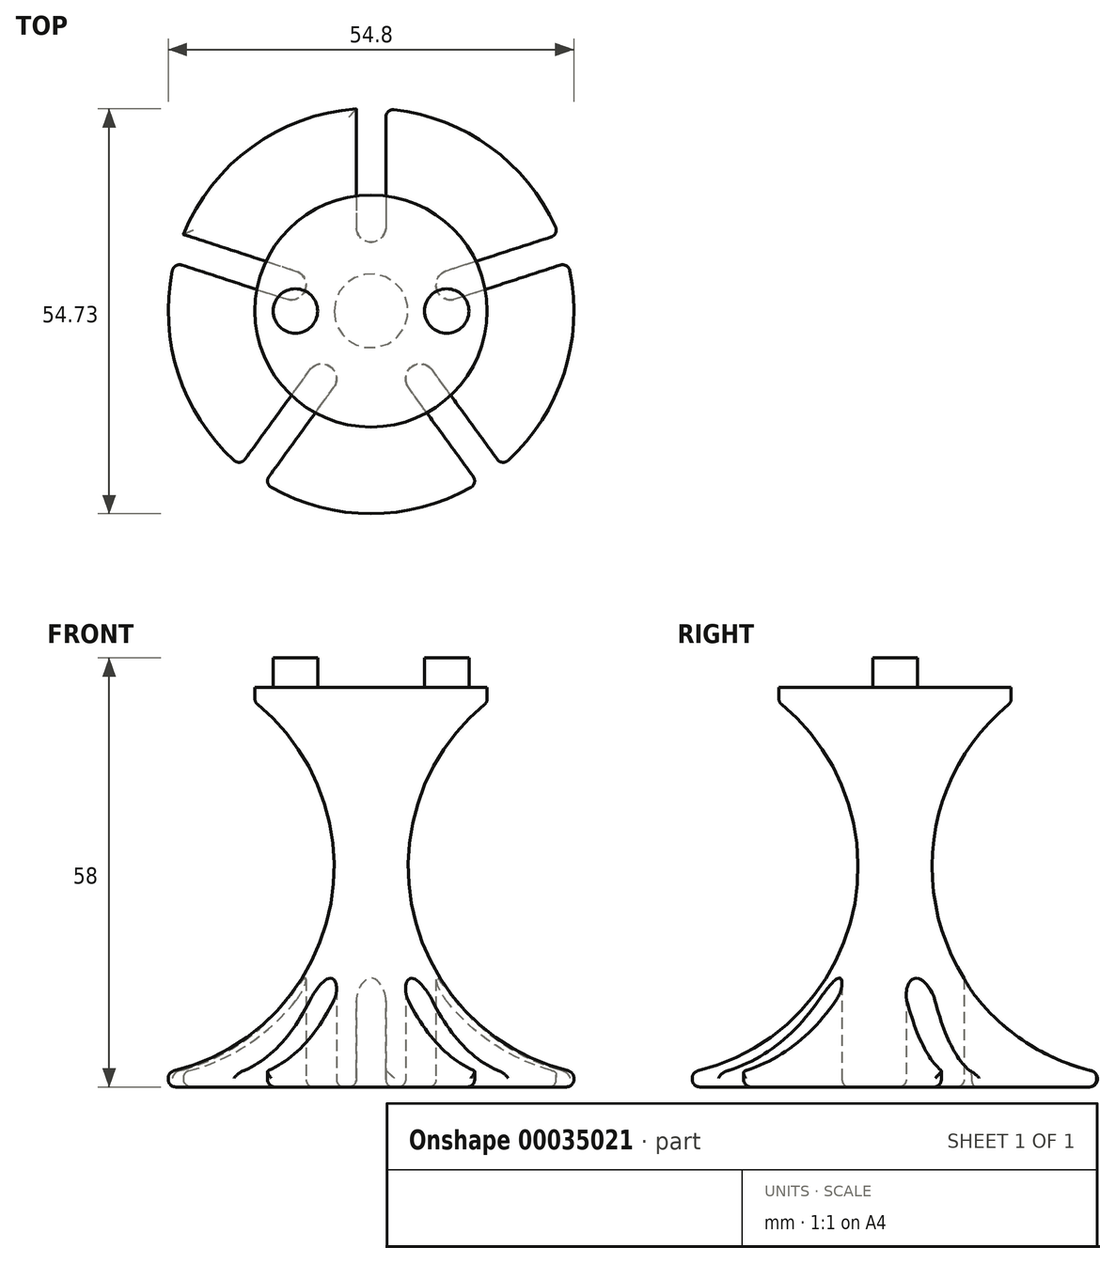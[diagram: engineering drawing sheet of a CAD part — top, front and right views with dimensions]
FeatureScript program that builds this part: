
annotation { "Feature Type Name" : "Feature", "Feature Type Description" : "" }
export const myFeature = defineFeature(function(context is Context, id is Id, definition is map)
    precondition{}
    {
        {
            var Q0;
            Q0=qCreatedBy(makeId("Front.planeOp"),FACE);
            var sketch = newSketch(context, id + "F0", { "sketchPlane" : qUnion([Q0])});
            skArc(sketch, "E0", {"start": v(-27.4, 0) * mm, "mid": v(-5.75, 21.3) * mm, "end": v(-15.7, 50) * mm});
            skLineSegment(sketch, "E1", {"start": v(-27.4, 0) * mm, "end": v(27.4, 0) * mm});
            skLineSegment(sketch, "E2", {"start": v(0, 0) * mm, "end": v(0, 50) * mm});
            skArc(sketch, "E3.MirrorCS", {"start": v(27.4, 0) * mm, "mid": v(5.75, 21.3) * mm, "end": v(15.7, 50) * mm});
            skLineSegment(sketch, "E4", {"start": v(15.7, 50) * mm, "end": v(-15.7, 50) * mm});
            skLineSegment(sketch, "E5", {"start": v(5.75, 21.3) * mm, "end": v(-5.75, 21.3) * mm, "construction": true});
            skLineSegment(sketch, "E6", {"start": v(-33.43, 27.78) * mm, "end": v(-33.43, 38) * mm, "construction": true});
            skSolve(sketch);
        }
        {
            var Q0;
            {var subQ1=sQuery(id+"F0.wireOp",EDGE,"E2");Q0=makeQuery(id+"F0.imprint","IMPRINT",FACE,{"disambiguationData":[TD([[makeQuery(id+"F0.imprint","IMPRINT",EDGE,{"derivedFrom":subQ1}),1.0]])]});}
            var Q1;
            Q1=sQuery(id+"F0.wireOp",EDGE,"E2");
            revolve(context, id + "F1", {"entities" : qUnion([Q0]), "axis" : qUnion([Q1]), "revolveType" : RevolveType.FULL});
        }
        {
            var Q0;
            Q0=makeQuery(id+"F1.opRevolve","SWEPT_FACE",FACE,{"disambiguationData":[OSD([sQuery(id+"F0.wireOp",EDGE,"E4")])]});
            var sketch = newSketch(context, id + "F2", { "sketchPlane" : qUnion([Q0])});
            skCircle(sketch, "E7", {"center": v(-10.22, 0) * mm, "radius": 3 * mm});
            skLineSegment(sketch, "E8", {"start": v(-7.22, 0) * mm, "end": v(0, 0) * mm, "construction": true});
            skCircle(sketch, "E9", {"center": v(10.22, 0) * mm, "radius": 3 * mm});
            skLineSegment(sketch, "E10", {"start": v(0, 0) * mm, "end": v(7.22, 0) * mm, "construction": true});
            skLineSegment(sketch, "E11", {"start": v(-8.9, 0) * mm, "end": v(-5.9, 0) * mm, "construction": true});
            skSolve(sketch);
        }
        {
            var Q0;
            Q0=makeQuery(id+"F2.imprint","IMPRINT",FACE,{"disambiguationData":[TD([[makeQuery(id+"F2.imprint","IMPRINT",EDGE,{"derivedFrom":sQuery(id+"F2.wireOp",EDGE,"E9")}),1.0]])]});
            var Q1;
            Q1=makeQuery(id+"F2.imprint","IMPRINT",FACE,{"disambiguationData":[TD([[makeQuery(id+"F2.imprint","IMPRINT",EDGE,{"derivedFrom":sQuery(id+"F2.wireOp",EDGE,"E7")}),1.0]])]});
            extrude(context, id + "F3", {"entities" : qUnion([Q0, Q1]), "operationType" : NewBodyOperationType.ADD, "depth" : 6 * mm});
        }
        {
            var Q0;
            Q0=makeQuery(id+"F1.opRevolve","SWEPT_FACE",FACE,{"disambiguationData":[OSD([sQuery(id+"F0.wireOp",EDGE,"E4")])]});
            extrude(context, id + "F4", {"entities" : qUnion([Q0]), "operationType" : NewBodyOperationType.ADD, "depth" : 2 * mm});
        }
        {
            var Q0;
            Q0=makeQuery(id+"F1.opRevolve","SWEPT_FACE",FACE,{"disambiguationData":[OSD([sQuery(id+"F0.wireOp",EDGE,"E1")])]});
            extrude(context, id + "F5", {"entities" : qUnion([Q0]), "operationType" : NewBodyOperationType.ADD, "depth" : 2 * mm});
        }
        {
            var Q0;
            Q0=makeQuery(id+"F5.opExtrude","CAP_FACE",FACE,{"disambiguationData":[OSD([sQuery(id+"F0.wireOp",EDGE,"E1")])],"isStart":false});
            var sketch = newSketch(context, id + "F6", { "sketchPlane" : qUnion([Q0])});
            skLineSegment(sketch, "E12", {"start": v(0, 0) * mm, "end": v(0, -27.4) * mm, "construction": true});
            skLineSegment(sketch, "E13", {"start": v(-2, -27.33) * mm, "end": v(-2, -11.33) * mm});
            skLineSegment(sketch, "E14", {"start": v(2, -27.33) * mm, "end": v(2, -11.33) * mm});
            skArc(sketch, "E15", {"start": v(2, -11.33) * mm, "mid": v(0, -9.33) * mm, "end": v(-2, -11.33) * mm});
            skLineSegment(sketch, "E16.1.0", {"start": v(25.37, -10.35) * mm, "end": v(10.15, -5.4) * mm});
            skArc(sketch, "E16.1.1", {"start": v(11.4, -1.6) * mm, "mid": v(8.87, -2.88) * mm, "end": v(10.15, -5.4) * mm});
            skLineSegment(sketch, "E16.1.2", {"start": v(26.6, -6.54) * mm, "end": v(11.4, -1.6) * mm});
            skLineSegment(sketch, "E16.2.0", {"start": v(17.68, 20.93) * mm, "end": v(8.28, 7.99) * mm});
            skArc(sketch, "E16.2.1", {"start": v(5.04, 10.34) * mm, "mid": v(5.48, 7.55) * mm, "end": v(8.28, 7.99) * mm});
            skLineSegment(sketch, "E16.2.2", {"start": v(14.44, 23.28) * mm, "end": v(5.04, 10.34) * mm});
            skLineSegment(sketch, "E16.3.0", {"start": v(-14.44, 23.28) * mm, "end": v(-5.04, 10.34) * mm});
            skArc(sketch, "E16.3.1", {"start": v(-8.28, 7.99) * mm, "mid": v(-5.48, 7.55) * mm, "end": v(-5.04, 10.34) * mm});
            skLineSegment(sketch, "E16.3.2", {"start": v(-17.68, 20.93) * mm, "end": v(-8.28, 7.99) * mm});
            skLineSegment(sketch, "E16.4.0", {"start": v(-26.6, -6.54) * mm, "end": v(-11.4, -1.6) * mm});
            skArc(sketch, "E16.4.1", {"start": v(-10.15, -5.4) * mm, "mid": v(-8.87, -2.88) * mm, "end": v(-11.4, -1.6) * mm});
            skLineSegment(sketch, "E16.4.2", {"start": v(-25.37, -10.35) * mm, "end": v(-10.15, -5.4) * mm});
            skPoint(sketch, "E16.center", {"position": v(0, 0) * mm});
            skSolve(sketch);
        }
        {
            var Q0;
            Q0 = qSketchRegion(id + "F6", true);
            var Q1;
            {var subQ2=sQuery(id+"F6.wireOp",EDGE,"E16.4.0");Q1=makeQuery(id+"F6.imprint","IMPRINT",FACE,{"disambiguationData":[TD([[makeQuery(id+"F6.imprint","IMPRINT",EDGE,{"derivedFrom":subQ2}),-1.0]])]});}
            var Q2;
            {var subQ2=sQuery(id+"F6.wireOp",EDGE,"E16.3.0");Q2=makeQuery(id+"F6.imprint","IMPRINT",FACE,{"disambiguationData":[TD([[makeQuery(id+"F6.imprint","IMPRINT",EDGE,{"derivedFrom":subQ2}),-1.0]])]});}
            var Q3;
            {var subQ2=sQuery(id+"F6.wireOp",EDGE,"E16.2.0");Q3=makeQuery(id+"F6.imprint","IMPRINT",FACE,{"disambiguationData":[TD([[makeQuery(id+"F6.imprint","IMPRINT",EDGE,{"derivedFrom":subQ2}),-1.0]])]});}
            var Q4;
            {var subQ2=sQuery(id+"F6.wireOp",EDGE,"E16.1.0");Q4=makeQuery(id+"F6.imprint","IMPRINT",FACE,{"disambiguationData":[TD([[makeQuery(id+"F6.imprint","IMPRINT",EDGE,{"derivedFrom":subQ2}),-1.0]])]});}
            var Q5;
            {var subQ2=sQuery(id+"F6.wireOp",EDGE,"E13");Q5=makeQuery(id+"F6.imprint","IMPRINT",FACE,{"disambiguationData":[TD([[makeQuery(id+"F6.imprint","IMPRINT",EDGE,{"derivedFrom":subQ2}),-1.0]])]});}
            extrude(context, id + "F7", {"entities" : qUnion([Q0, Q1, Q2, Q3, Q4, Q5]), "operationType" : NewBodyOperationType.REMOVE, "endBound" : BoundingType.UP_TO_NEXT, "oppositeDirection" : true, "depth" : 25 * mm});
        }
        {
            var Q0;
            {var subQ0=sQuery(id+"F0.wireOp",EDGE,"E0");var subQ1=sQuery(id+"F0.wireOp",EDGE,"E4");Q0=makeQuery(id+"F4.boolean.opBoolean","MERGE",EDGE,{"derivedFrom":[makeQuery(id+"F1.opRevolve","SWEPT_EDGE",EDGE,{"disambiguationData":[OSD([subQ0,subQ1])]}),makeQuery(id+"F4.opExtrude","CAP_EDGE",EDGE,{"disambiguationData":[OSD([subQ0,subQ1])],"isStart":true})]});}
            var Q1;
            Q1=makeQuery(id+"F5.opExtrude","CAP_FACE",FACE,{"disambiguationData":[OSD([sQuery(id+"F0.wireOp",EDGE,"E1")])],"isStart":false});
            var Q2;
            {var subQ0=sQuery(id+"F0.wireOp",EDGE,"E0");var subQ1=sQuery(id+"F0.wireOp",EDGE,"E1");Q2=makeQuery(id+"F7.boolean.opBoolean","SPLIT",EDGE,{"disambiguationData":[TD([makeQuery(id+"F7.opExtrude","SWEPT_FACE",FACE,{"disambiguationData":[OSD([sQuery(id+"F6.wireOp",EDGE,"E16.3.2")])]})])],"derivedFrom":makeQuery(id+"F5.boolean.opBoolean","MERGE",EDGE,{"derivedFrom":[makeQuery(id+"F1.opRevolve","SWEPT_EDGE",EDGE,{"disambiguationData":[OSD([subQ0,subQ1])]}),makeQuery(id+"F5.opExtrude","CAP_EDGE",EDGE,{"disambiguationData":[OSD([subQ0,subQ1])],"isStart":true})]})});}
            var Q3;
            {var subQ0=sQuery(id+"F0.wireOp",EDGE,"E0");var subQ1=sQuery(id+"F0.wireOp",EDGE,"E1");Q3=makeQuery(id+"F7.boolean.opBoolean","SPLIT",EDGE,{"disambiguationData":[TD([makeQuery(id+"F7.opExtrude","SWEPT_FACE",FACE,{"disambiguationData":[OSD([sQuery(id+"F6.wireOp",EDGE,"E16.2.2")])]})])],"derivedFrom":makeQuery(id+"F5.boolean.opBoolean","MERGE",EDGE,{"derivedFrom":[makeQuery(id+"F1.opRevolve","SWEPT_EDGE",EDGE,{"disambiguationData":[OSD([subQ0,subQ1])]}),makeQuery(id+"F5.opExtrude","CAP_EDGE",EDGE,{"disambiguationData":[OSD([subQ0,subQ1])],"isStart":true})]})});}
            var Q4;
            {var subQ0=sQuery(id+"F0.wireOp",EDGE,"E0");var subQ1=sQuery(id+"F0.wireOp",EDGE,"E1");Q4=makeQuery(id+"F7.boolean.opBoolean","SPLIT",EDGE,{"disambiguationData":[TD([makeQuery(id+"F7.opExtrude","SWEPT_FACE",FACE,{"disambiguationData":[OSD([sQuery(id+"F6.wireOp",EDGE,"E16.1.2")])]})])],"derivedFrom":makeQuery(id+"F5.boolean.opBoolean","MERGE",EDGE,{"derivedFrom":[makeQuery(id+"F1.opRevolve","SWEPT_EDGE",EDGE,{"disambiguationData":[OSD([subQ0,subQ1])]}),makeQuery(id+"F5.opExtrude","CAP_EDGE",EDGE,{"disambiguationData":[OSD([subQ0,subQ1])],"isStart":true})]})});}
            var Q5;
            {var subQ0=sQuery(id+"F0.wireOp",EDGE,"E0");var subQ1=sQuery(id+"F0.wireOp",EDGE,"E1");Q5=makeQuery(id+"F7.boolean.opBoolean","SPLIT",EDGE,{"disambiguationData":[TD([makeQuery(id+"F7.opExtrude","SWEPT_FACE",FACE,{"disambiguationData":[OSD([sQuery(id+"F6.wireOp",EDGE,"E14")])]})])],"derivedFrom":makeQuery(id+"F5.boolean.opBoolean","MERGE",EDGE,{"derivedFrom":[makeQuery(id+"F1.opRevolve","SWEPT_EDGE",EDGE,{"disambiguationData":[OSD([subQ0,subQ1])]}),makeQuery(id+"F5.opExtrude","CAP_EDGE",EDGE,{"disambiguationData":[OSD([subQ0,subQ1])],"isStart":true})]})});}
            var Q6;
            {var subQ0=sQuery(id+"F0.wireOp",EDGE,"E0");var subQ1=sQuery(id+"F0.wireOp",EDGE,"E1");Q6=makeQuery(id+"F7.boolean.opBoolean","SPLIT",EDGE,{"disambiguationData":[TD([makeQuery(id+"F7.opExtrude","SWEPT_FACE",FACE,{"disambiguationData":[OSD([sQuery(id+"F6.wireOp",EDGE,"E13")])]})])],"derivedFrom":makeQuery(id+"F5.boolean.opBoolean","MERGE",EDGE,{"derivedFrom":[makeQuery(id+"F1.opRevolve","SWEPT_EDGE",EDGE,{"disambiguationData":[OSD([subQ0,subQ1])]}),makeQuery(id+"F5.opExtrude","CAP_EDGE",EDGE,{"disambiguationData":[OSD([subQ0,subQ1])],"isStart":true})]})});}
            var Q7;
            Q7=makeQuery(id+"F7.boolean.opBoolean","COPY",EDGE,{"derivedFrom":makeQuery(id+"F7.opExtrude","SWEPT_EDGE",EDGE,{"disambiguationData":[OSD([sQuery(id+"F0.wireOp",EDGE,"E0"),sQuery(id+"F0.wireOp",EDGE,"E1"),sQuery(id+"F6.wireOp",EDGE,"E13")])]})});
            var Q8;
            Q8=makeQuery(id+"F7.boolean.opBoolean","COPY",EDGE,{"derivedFrom":makeQuery(id+"F7.opExtrude","SWEPT_EDGE",EDGE,{"disambiguationData":[OSD([sQuery(id+"F0.wireOp",EDGE,"E0"),sQuery(id+"F0.wireOp",EDGE,"E1"),sQuery(id+"F6.wireOp",EDGE,"E14")])]})});
            var Q9;
            Q9=makeQuery(id+"F7.boolean.opBoolean","COPY",EDGE,{"derivedFrom":makeQuery(id+"F7.opExtrude","SWEPT_EDGE",EDGE,{"disambiguationData":[OSD([sQuery(id+"F0.wireOp",EDGE,"E0"),sQuery(id+"F0.wireOp",EDGE,"E1"),sQuery(id+"F6.wireOp",EDGE,"E16.1.0")])]})});
            var Q10;
            Q10=makeQuery(id+"F7.boolean.opBoolean","COPY",EDGE,{"derivedFrom":makeQuery(id+"F7.opExtrude","SWEPT_EDGE",EDGE,{"disambiguationData":[OSD([sQuery(id+"F0.wireOp",EDGE,"E0"),sQuery(id+"F0.wireOp",EDGE,"E1"),sQuery(id+"F6.wireOp",EDGE,"E16.1.2")])]})});
            var Q11;
            Q11=makeQuery(id+"F7.boolean.opBoolean","COPY",EDGE,{"derivedFrom":makeQuery(id+"F7.opExtrude","SWEPT_EDGE",EDGE,{"disambiguationData":[OSD([sQuery(id+"F0.wireOp",EDGE,"E0"),sQuery(id+"F0.wireOp",EDGE,"E1"),sQuery(id+"F6.wireOp",EDGE,"E16.2.0")])]})});
            var Q12;
            Q12=makeQuery(id+"F7.boolean.opBoolean","COPY",EDGE,{"derivedFrom":makeQuery(id+"F7.opExtrude","SWEPT_EDGE",EDGE,{"disambiguationData":[OSD([sQuery(id+"F0.wireOp",EDGE,"E0"),sQuery(id+"F0.wireOp",EDGE,"E1"),sQuery(id+"F6.wireOp",EDGE,"E16.2.2")])]})});
            var Q13;
            Q13=makeQuery(id+"F7.boolean.opBoolean","COPY",EDGE,{"derivedFrom":makeQuery(id+"F7.opExtrude","SWEPT_EDGE",EDGE,{"disambiguationData":[OSD([sQuery(id+"F0.wireOp",EDGE,"E0"),sQuery(id+"F0.wireOp",EDGE,"E1"),sQuery(id+"F6.wireOp",EDGE,"E16.3.0")])]})});
            var Q14;
            Q14=makeQuery(id+"F7.boolean.opBoolean","COPY",EDGE,{"derivedFrom":makeQuery(id+"F7.opExtrude","SWEPT_EDGE",EDGE,{"disambiguationData":[OSD([sQuery(id+"F0.wireOp",EDGE,"E0"),sQuery(id+"F0.wireOp",EDGE,"E1"),sQuery(id+"F6.wireOp",EDGE,"E16.3.2")])]})});
            var Q15;
            {var subQ0=sQuery(id+"F0.wireOp",EDGE,"E0");var subQ1=sQuery(id+"F0.wireOp",EDGE,"E1");Q15=makeQuery(id+"F7.boolean.opBoolean","SPLIT",FACE,{"disambiguationData":[TD([makeQuery(id+"F7.opExtrude","SWEPT_FACE",FACE,{"disambiguationData":[OSD([sQuery(id+"F6.wireOp",EDGE,"E16.3.2")])]})])],"derivedFrom":makeQuery(id+"F5.opExtrude","SWEPT_FACE",FACE,{"disambiguationData":[OSD([subQ0,subQ1])]})});}
            var Q16;
            Q16=makeQuery(id+"F7.boolean.opBoolean","COPY",EDGE,{"derivedFrom":makeQuery(id+"F7.opExtrude","SWEPT_EDGE",EDGE,{"disambiguationData":[OSD([sQuery(id+"F0.wireOp",EDGE,"E0"),sQuery(id+"F0.wireOp",EDGE,"E1"),sQuery(id+"F6.wireOp",EDGE,"E16.4.2")])]})});
            var Q17;
            Q17=makeQuery(id+"F7.boolean.opBoolean","COPY",EDGE,{"derivedFrom":makeQuery(id+"F7.opExtrude","TWEAK_EDGE",EDGE,{"derivedFrom":[makeQuery(id+"F1.opRevolve","SWEPT_FACE",FACE,{"disambiguationData":[OSD([sQuery(id+"F0.wireOp",EDGE,"E0")])]}),makeQuery(id+"F6.imprint","IMPRINT",EDGE,{"derivedFrom":sQuery(id+"F6.wireOp",EDGE,"E16.4.1")})]})});
            var Q18;
            Q18=makeQuery(id+"F7.boolean.opBoolean","COPY",EDGE,{"derivedFrom":makeQuery(id+"F7.opExtrude","TWEAK_EDGE",EDGE,{"derivedFrom":[makeQuery(id+"F1.opRevolve","SWEPT_FACE",FACE,{"disambiguationData":[OSD([sQuery(id+"F0.wireOp",EDGE,"E0")])]}),makeQuery(id+"F6.imprint","IMPRINT",EDGE,{"derivedFrom":sQuery(id+"F6.wireOp",EDGE,"E16.3.1")})]})});
            var Q19;
            Q19=makeQuery(id+"F7.boolean.opBoolean","COPY",EDGE,{"derivedFrom":makeQuery(id+"F7.opExtrude","TWEAK_EDGE",EDGE,{"derivedFrom":[makeQuery(id+"F1.opRevolve","SWEPT_FACE",FACE,{"disambiguationData":[OSD([sQuery(id+"F0.wireOp",EDGE,"E0")])]}),makeQuery(id+"F6.imprint","IMPRINT",EDGE,{"derivedFrom":sQuery(id+"F6.wireOp",EDGE,"E16.2.1")})]})});
            var Q20;
            Q20=makeQuery(id+"F7.boolean.opBoolean","COPY",EDGE,{"derivedFrom":makeQuery(id+"F7.opExtrude","TWEAK_EDGE",EDGE,{"derivedFrom":[makeQuery(id+"F1.opRevolve","SWEPT_FACE",FACE,{"disambiguationData":[OSD([sQuery(id+"F0.wireOp",EDGE,"E0")])]}),makeQuery(id+"F6.imprint","IMPRINT",EDGE,{"derivedFrom":sQuery(id+"F6.wireOp",EDGE,"E16.1.1")})]})});
            var Q21;
            Q21=makeQuery(id+"F7.boolean.opBoolean","COPY",EDGE,{"derivedFrom":makeQuery(id+"F7.opExtrude","TWEAK_EDGE",EDGE,{"derivedFrom":[makeQuery(id+"F1.opRevolve","SWEPT_FACE",FACE,{"disambiguationData":[OSD([sQuery(id+"F0.wireOp",EDGE,"E0")])]}),makeQuery(id+"F6.imprint","IMPRINT",EDGE,{"derivedFrom":sQuery(id+"F6.wireOp",EDGE,"E15")})]})});
            fillet(context, id + "F8", {"entities" : qUnion([Q0, Q1, Q2, Q3, Q4, Q5, Q6, Q7, Q8, Q9, Q10, Q11, Q12, Q13, Q14, Q15, Q16, Q17, Q18, Q19, Q20, Q21]), "radius" : 1 * mm, "tangentPropagation" : true, "allowEdgeOverflow" : false});
        }
    });
